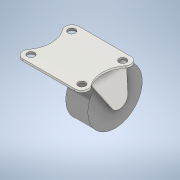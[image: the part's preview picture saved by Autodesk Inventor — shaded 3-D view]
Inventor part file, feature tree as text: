
AUTODESK INVENTOR PART (.ipt)
format: ipt  version: 2021 (Build 250183000, 183)  size: 204,800 bytes
history: native  units: mm
features: extrude x5, sketch x4, revolve x1, mirror x1
ambient origin geometry x8: Origin, YZ Plane, XZ Plane, XY Plane, X Axis, Y Axis, Z Axis, Center Point
bodies: Volumenkörper1 (feature_tree)
feature tree (11):
  extrude  "Extrusion1"  Depth=4.0mm
  sketch  "Skizze2"  dims[d2=24.0mm d3=33.0mm]
  revolve  "Umdrehung1"
  extrude  "Extrusion2"  Depth=33.0mm
  extrude  "Extrusion3"  Depth=38.5mm
  extrude  "Extrusion4"  Depth=3.0mm
  mirror  "Spiegeln1"
  extrude  "Extrusion5"  Depth=1.2mm
  sketch  "Skizze1"  dims[d0=4.0mm d1=30.0mm]
  sketch  "Skizze3"  dims[d4=4.3mm d5=38.5mm]
  sketch  "Skizze4"  dims[d6=1.2mm d7=0.0mm d8=3.0mm d9=32.0mm d10=40.8mm d12=0.0mm d13=10.0mm d14=8.0mm d16=8.0mm d18=24.0mm d20=90.0deg d21=13.0mm d22=0.0mm d23=18.0mm d24=0.0mm d25=1.2mm d26=0.0mm d27=1.2mm d28=1.2mm d29=0.0mm]
